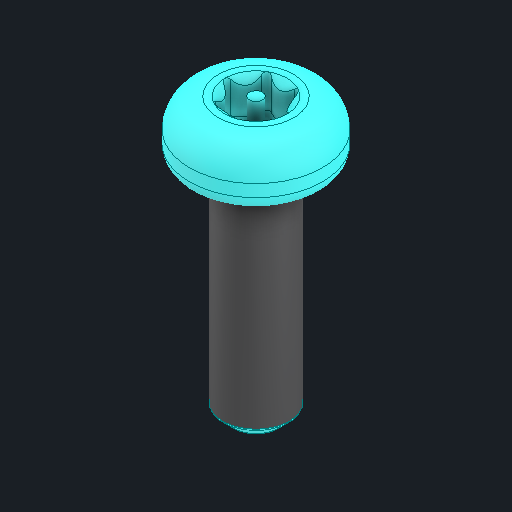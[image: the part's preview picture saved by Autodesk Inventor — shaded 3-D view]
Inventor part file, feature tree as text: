
AUTODESK INVENTOR PART (.ipt)
format: ipt  version: 2025 (Build 290162000, 162)  size: 174,080 bytes
history: native  units: in
note: dims shown in document units (in); Inventor stores cm internally (conversion verified against a paired STEP export)
features: fillet x1
ambient origin geometry x8: Origin, YZ Plane, XZ Plane, XY Plane, X Axis, Y Axis, Z Axis, Center Point
bodies: Solid1 (feature_tree)
feature tree (1):
  fillet  "Fillet3"  [1 undecoded]
note: 1 required parameter value undecoded (feature->parameter linkage not recoverable at this tier; creation-order binding heuristic only, values carry confidence <= 0.55)
